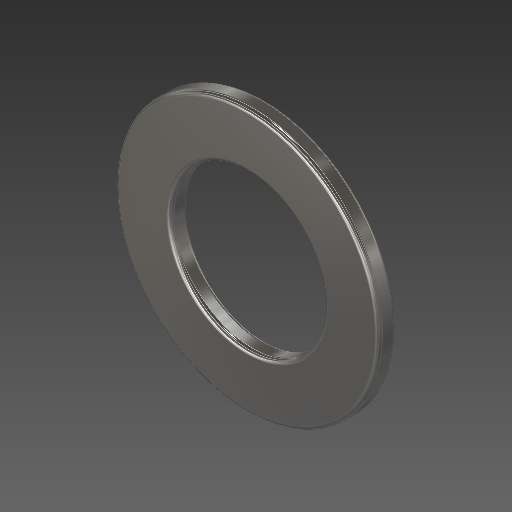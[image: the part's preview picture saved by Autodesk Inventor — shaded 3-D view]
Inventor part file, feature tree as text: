
AUTODESK INVENTOR PART (.ipt)
format: ipt  version: 2018 (Build 220112000, 112)  size: 154,624 bytes
history: native  units: mm
features: extrude x1, fillet x1, sketch x1
ambient origin geometry x8: Origin, YZ Plane, XZ Plane, XY Plane, X Axis, Y Axis, Z Axis, Center Point
bodies: Solid1 (feature_tree)
feature tree (3):
  extrude  "Extrusion1"  Depth=0.5mm
  fillet  "Fillet1"  Radius=2.0mm
  sketch  "Sketch1"  dims[d0=29.0mm d1=16.8mm d2=2.0mm d3=0.0mm d4=0.5mm]
